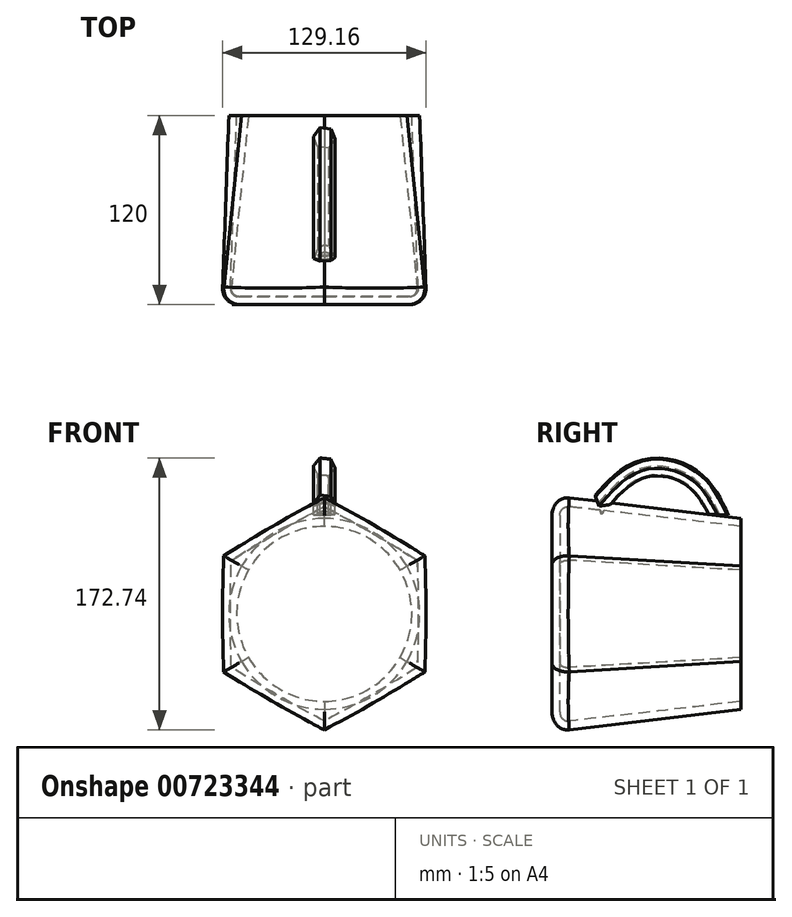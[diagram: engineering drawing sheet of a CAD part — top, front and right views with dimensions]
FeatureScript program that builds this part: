
annotation { "Feature Type Name" : "Feature", "Feature Type Description" : "" }
export const myFeature = defineFeature(function(context is Context, id is Id, definition is map)
    precondition{}
    {
        {
            var Q0;
            Q0=qCreatedBy(makeId("Front.planeOp"),FACE);
            cPlane(context, id + "F0", {"entities" : qUnion([Q0]), "cplaneType" : CPlaneType.OFFSET, "offset" : 120 * mm, "width" : 150 * mm, "height" : 150 * mm});
        }
        {
            var Q0;
            Q0=qCreatedBy(makeId("Front.planeOp"),FACE);
            var sketch = newSketch(context, id + "F1", { "sketchPlane" : qUnion([Q0])});
            skCircle(sketch, "E0", {"center": v(0, 0) * mm, "radius": 60.59 * mm});
            skSolve(sketch);
        }
        {
            var Q0;
            Q0=qCreatedBy(id+"F0.planeOp",FACE);
            var sketch = newSketch(context, id + "F2", { "sketchPlane" : qUnion([Q0])});
            skLineSegment(sketch, "E1.bottom", {"start": v(-75, -75) * mm, "end": v(75, -75) * mm});
            skLineSegment(sketch, "E1.top", {"start": v(-75, 75) * mm, "end": v(75, 75) * mm});
            skLineSegment(sketch, "E1.left", {"start": v(-75, -75) * mm, "end": v(-75, 75) * mm});
            skLineSegment(sketch, "E1.right", {"start": v(75, -75) * mm, "end": v(75, 75) * mm});
            skPoint(sketch, "E1.middle", {"position": v(0, 0) * mm});
            skCircle(sketch, "E2.cCircle", {"center": v(0, 0) * mm, "radius": 75 * mm, "construction": true});
            skLineSegment(sketch, "E2.0", {"start": v(0, -75) * mm, "end": v(-64.95, -37.5) * mm});
            skLineSegment(sketch, "E2.1", {"start": v(-64.95, -37.5) * mm, "end": v(-64.95, 37.5) * mm});
            skLineSegment(sketch, "E2.2", {"start": v(-64.95, 37.5) * mm, "end": v(0, 75) * mm});
            skLineSegment(sketch, "E2.3", {"start": v(0, 75) * mm, "end": v(64.95, 37.5) * mm});
            skLineSegment(sketch, "E2.4", {"start": v(64.95, 37.5) * mm, "end": v(64.95, -37.5) * mm});
            skLineSegment(sketch, "E2.5", {"start": v(64.95, -37.5) * mm, "end": v(0, -75) * mm});
            skSolve(sketch);
        }
        {
            var Q0;
            Q0=makeQuery(id+"F1.imprint","IMPRINT",FACE,{"disambiguationData":[TD([[makeQuery(id+"F1.imprint","IMPRINT",EDGE,{"derivedFrom":sQuery(id+"F1.wireOp",EDGE,"E0")}),1.0]])]});
            var Q1;
            Q1=makeQuery(id+"F2.imprint","IMPRINT",FACE,{"disambiguationData":[TD([[makeQuery(id+"F2.imprint","IMPRINT",EDGE,{"derivedFrom":sQuery(id+"F2.wireOp",EDGE,"E2.0")}),-1.0]])]});
            loft(context, id + "F3", {"sheetProfilesArray" : [{ "sheetProfileEntities" : qUnion([Q0]) }, { "sheetProfileEntities" : qUnion([Q1]) }]});
        }
        {
            var Q0;
            Q0=makeQuery(id+"F3.opLoft","CAP_FACE",FACE,{"disambiguationData":[OSD([makeQuery(id+"F2.imprint","IMPRINT",FACE,{"disambiguationData":[TD([[makeQuery(id+"F2.imprint","IMPRINT",EDGE,{"derivedFrom":sQuery(id+"F2.wireOp",EDGE,"E2.0")}),-1.0]])]})])],"isStart":true});
            fillet(context, id + "F4", {"entities" : qUnion([Q0]), "radius" : 10 * mm, "tangentPropagation" : true, "allowEdgeOverflow" : false});
        }
        {
            var Q0;
            Q0=makeQuery(id+"F3.opLoft","CAP_FACE",FACE,{"disambiguationData":[OSD([makeQuery(id+"F1.imprint","IMPRINT",FACE,{"disambiguationData":[TD([[makeQuery(id+"F1.imprint","IMPRINT",EDGE,{"derivedFrom":sQuery(id+"F1.wireOp",EDGE,"E0")}),1.0]])]})])],"isStart":true});
            shell(context, id + "F5", {"entities" : qUnion([Q0]), "thickness" : 5 * mm});
        }
        {
            var Q0;
            Q0=qCreatedBy(makeId("Right.planeOp"),FACE);
            var sketch = newSketch(context, id + "F6", { "sketchPlane" : qUnion([Q0])});
            skFitSpline(sketch, "E3", {"points": [v(-89.38, 65.78) * mm, v(-62.2, 88.53) * mm, v(-32.88, 83.38) * mm, v(-17.83, 63.18) * mm], "startDerivative": vector(60.3, 67) * mm, "endDerivative": vector(36.79, -72.05) * mm});
            skSolve(sketch);
        }
        {
            var Q0;
            Q0=qCreatedBy(makeId("Top.planeOp"),FACE);
            cPlane(context, id + "F7", {"entities" : qUnion([Q0]), "cplaneType" : CPlaneType.OFFSET, "offset" : 70 * mm, "width" : 150 * mm, "height" : 150 * mm});
        }
        {
            var Q0;
            Q0=qCreatedBy(id+"F7.planeOp",FACE);
            var sketch = newSketch(context, id + "F8", { "sketchPlane" : qUnion([Q0])});
            skCircle(sketch, "E4.cCircle", {"center": v(0, -17.83) * mm, "radius": 6.98 * mm, "construction": true});
            skLineSegment(sketch, "E4.0", {"start": v(-6.93, -17.03) * mm, "end": v(-2.78, -11.43) * mm});
            skLineSegment(sketch, "E4.1", {"start": v(-2.78, -11.43) * mm, "end": v(4.15, -12.22) * mm});
            skLineSegment(sketch, "E4.2", {"start": v(4.15, -12.22) * mm, "end": v(6.93, -18.62) * mm});
            skLineSegment(sketch, "E4.3", {"start": v(6.93, -18.62) * mm, "end": v(2.78, -24.22) * mm});
            skLineSegment(sketch, "E4.4", {"start": v(2.78, -24.22) * mm, "end": v(-4.15, -23.43) * mm});
            skLineSegment(sketch, "E4.5", {"start": v(-4.15, -23.43) * mm, "end": v(-6.93, -17.03) * mm});
            skSolve(sketch);
        }
        {
            var Q0;
            Q0=makeQuery(id+"F8.imprint","IMPRINT",FACE,{"disambiguationData":[TD([[makeQuery(id+"F8.imprint","IMPRINT",EDGE,{"derivedFrom":sQuery(id+"F8.wireOp",EDGE,"E4.0")}),-1.0]])]});
            var Q1;
            Q1=sQuery(id+"F6.wireOp",EDGE,"E3");
            sweep(context, id + "F9", {"operationType" : NewBodyOperationType.ADD, "profiles" : qUnion([Q0]), "path" : qUnion([Q1])});
        }
    });
